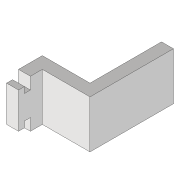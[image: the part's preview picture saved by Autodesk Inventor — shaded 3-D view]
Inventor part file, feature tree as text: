
AUTODESK INVENTOR PART (.ipt)
format: ipt  version: 2020 (Build 240168000, 168)  size: 163,840 bytes
history: native  units: mm
features: extrude x5, sketch x5, projected_geometry x2
ambient origin geometry x8: Origin, YZ Plane, XZ Plane, XY Plane, X Axis, Y Axis, Z Axis, Center Point
bodies: Volumenkörper1 (feature_tree)
feature tree (12):
  extrude  "Extrusion1"  Depth=20.0mm
  extrude  "Extrusion3"  Depth=5.0mm
  extrude  "Extrusion4"  TaperAngle=90.0deg  [1 undecoded]
  extrude  "Extrusion5"  Depth=10.0mm TaperAngle=0.0deg
  extrude  "Extrusion6"  Depth=10.0mm
  sketch  "Skizze1"  dims[d0=30.0mm d1=20.0mm]
  sketch  "Skizze3"  dims[d2=5.0mm d3=5.0mm]
  sketch  "Skizze4"  dims[d4=20.0mm d5=90.0deg]
  sketch  "Skizze5"  dims[d6=40.0mm d7=10.0mm d8=0.0mm]
  sketch  "Skizze6"  dims[d12=10.0mm d13=10.0mm d14=10.0mm d15=60.0mm d16=50.0mm d17=60.0mm d18=17.75mm d19=0.0mm d20=200.0mm d21=180.0mm d22=30.0deg d23=30.0deg d24=40.0mm d25=20.0mm d26=15.25mm d27=0.0mm d28=20.25mm d29=0.0mm d30=140.0mm d31=90.0mm d32=0.0mm]
  projected_geometry  "Projizierte Kontur1"
  projected_geometry  "Projizierte Kontur2"
note: 1 required parameter value undecoded (feature->parameter linkage not recoverable at this tier; creation-order binding heuristic only, values carry confidence <= 0.55)
